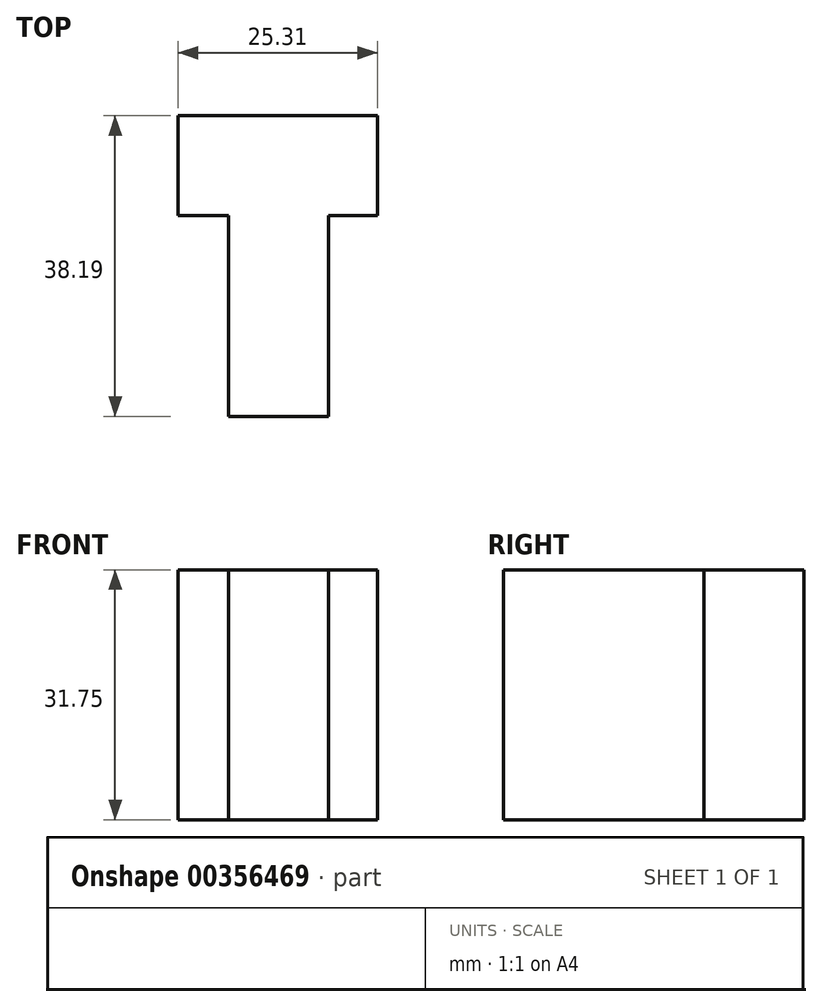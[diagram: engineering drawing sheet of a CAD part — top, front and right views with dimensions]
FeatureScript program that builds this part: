
annotation { "Feature Type Name" : "Feature", "Feature Type Description" : "" }
export const myFeature = defineFeature(function(context is Context, id is Id, definition is map)
    precondition{}
    {
        {
            var Q0;
            Q0=qCreatedBy(makeId("Top.planeOp"),FACE);
            var sketch = newSketch(context, id + "F0", { "sketchPlane" : qUnion([Q0])});
            skLineSegment(sketch, "E0", {"start": v(-32.7, 0) * mm, "end": v(-32.7, 25.5) * mm});
            skLineSegment(sketch, "E1", {"start": v(-32.7, 25.5) * mm, "end": v(-39.13, 25.5) * mm});
            skLineSegment(sketch, "E2", {"start": v(-39.13, 25.5) * mm, "end": v(-39.13, 38.2) * mm});
            skLineSegment(sketch, "E3", {"start": v(-39.13, 38.2) * mm, "end": v(-13.82, 38.2) * mm});
            skLineSegment(sketch, "E4", {"start": v(-13.82, 38.2) * mm, "end": v(-13.82, 25.5) * mm});
            skLineSegment(sketch, "E5", {"start": v(-13.82, 25.5) * mm, "end": v(-20.05, 25.5) * mm});
            skLineSegment(sketch, "E6", {"start": v(-20.05, 25.5) * mm, "end": v(-20.05, 0) * mm});
            skLineSegment(sketch, "E7", {"start": v(-32.7, 0) * mm, "end": v(-20.05, 0) * mm});
            skSolve(sketch);
        }
        {
            var Q0;
            Q0 = qSketchRegion(id + "F0", true);
            extrude(context, id + "F1", {"entities" : qUnion([Q0]), "depth" : 31.75 * mm});
        }
    });
